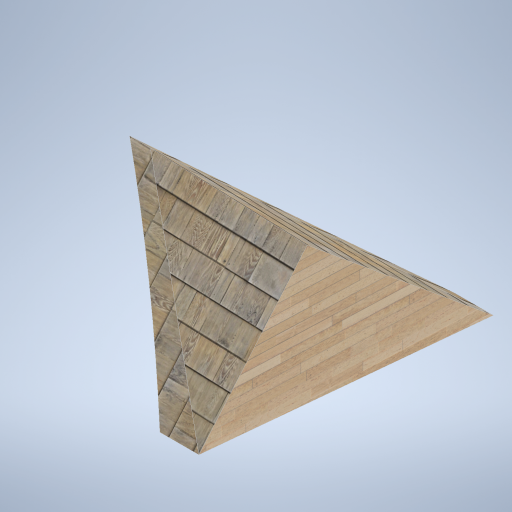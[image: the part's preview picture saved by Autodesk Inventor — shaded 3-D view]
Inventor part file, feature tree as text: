
AUTODESK INVENTOR PART (.ipt)
format: ipt  version: 2024.2 (Build 282272000, 272)  size: 408,064 bytes
history: native  units: in
note: dims shown in document units (in); Inventor stores cm internally (conversion verified against a paired STEP export)
features: sketch x6, plane x5, other x3
ambient origin geometry x8: Origin, YZ Plane, XZ Plane, XY Plane, X Axis, Y Axis, Z Axis, Center Point
bodies: Solid1 (feature_tree)
feature tree (14):
  other  "panel_pad_03.ipt"
  other  "Solid1::panel_pad_03.ipt"
  other  "TaggingFeature1"
  sketch  "Sketch1"  dims[d0=0.3937in]
  sketch  "Sketch2"
  sketch  "Sketch3"
  sketch  "Sketch6"
  sketch  "Sketch7"
  sketch  "Sketch8"
  plane  "Work Plane1"
  plane  "Work Plane2"
  plane  "Work Plane3"
  plane  "Work Plane4"
  plane  "Work Plane5"
